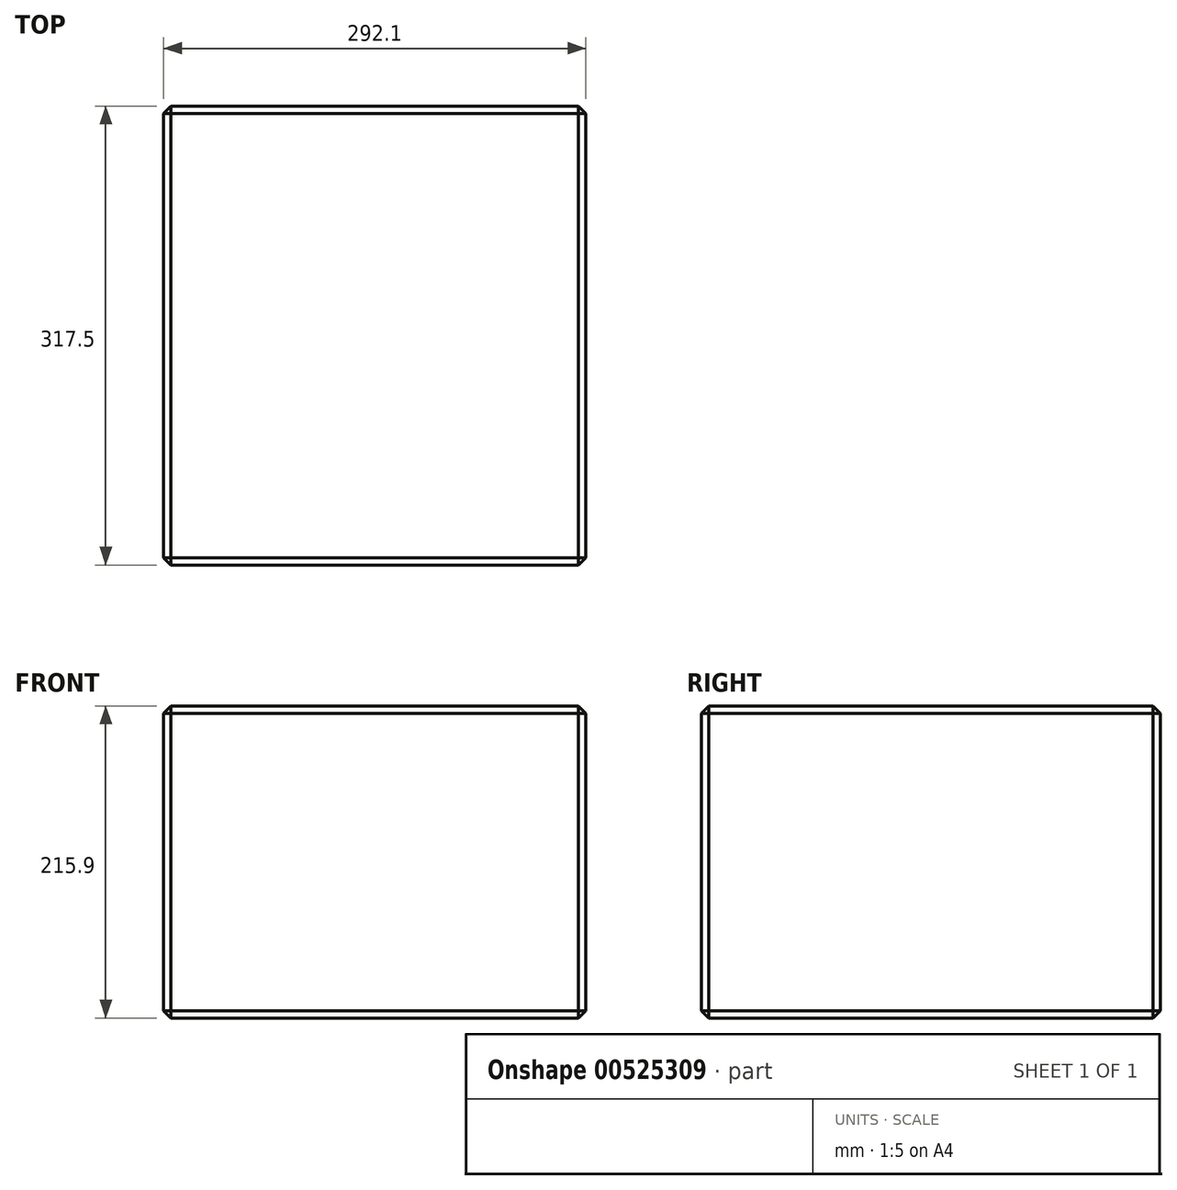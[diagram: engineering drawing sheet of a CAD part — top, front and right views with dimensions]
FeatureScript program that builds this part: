
annotation { "Feature Type Name" : "Feature", "Feature Type Description" : "" }
export const myFeature = defineFeature(function(context is Context, id is Id, definition is map)
    precondition{}
    {
        {
            var Q0;
            Q0=qCreatedBy(makeId("Top.planeOp"),FACE);
            var sketch = newSketch(context, id + "F0", { "sketchPlane" : qUnion([Q0])});
            skLineSegment(sketch, "E0.bottom", {"start": v(0, 0) * mm, "end": v(292.1, 0) * mm});
            skLineSegment(sketch, "E0.top", {"start": v(0, 317.5) * mm, "end": v(292.1, 317.5) * mm});
            skLineSegment(sketch, "E0.left", {"start": v(0, 0) * mm, "end": v(0, 317.5) * mm});
            skLineSegment(sketch, "E0.right", {"start": v(292.1, 0) * mm, "end": v(292.1, 317.5) * mm});
            skSolve(sketch);
        }
        {
            var Q0;
            Q0=makeQuery(id+"F0.imprint","IMPRINT",FACE,{"disambiguationData":[TD([[makeQuery(id+"F0.imprint","IMPRINT",EDGE,{"derivedFrom":sQuery(id+"F0.wireOp",EDGE,"E0.bottom")}),1.0]])]});
            extrude(context, id + "F1", {"entities" : qUnion([Q0]), "depth" : 215.9 * mm, "offsetDistance" : 25.4 * mm});
        }
        {
            var Q0;
            Q0=makeQuery(id+"F1.opExtrude","CAP_FACE",FACE,{"disambiguationData":[OSD([sQuery(id+"F0.wireOp",EDGE,"E0.bottom"),sQuery(id+"F0.wireOp",EDGE,"E0.top"),sQuery(id+"F0.wireOp",EDGE,"E0.left"),sQuery(id+"F0.wireOp",EDGE,"E0.right")])],"isStart":false});
            var Q1;
            Q1=makeQuery(id+"F1.opExtrude","SWEPT_FACE",FACE,{"disambiguationData":[OSD([sQuery(id+"F0.wireOp",EDGE,"E0.bottom")])]});
            var Q2;
            Q2=makeQuery(id+"F1.opExtrude","SWEPT_FACE",FACE,{"disambiguationData":[OSD([sQuery(id+"F0.wireOp",EDGE,"E0.right")])]});
            var Q3;
            Q3=makeQuery(id+"F1.opExtrude","SWEPT_FACE",FACE,{"disambiguationData":[OSD([sQuery(id+"F0.wireOp",EDGE,"E0.top")])]});
            var Q4;
            Q4=makeQuery(id+"F1.opExtrude","SWEPT_FACE",FACE,{"disambiguationData":[OSD([sQuery(id+"F0.wireOp",EDGE,"E0.left")])]});
            chamfer(context, id + "F2", {"entities" : qUnion([Q0, Q1, Q2, Q3, Q4]), "width" : 5.08 * mm, "tangentPropagation" : true});
        }
    });
